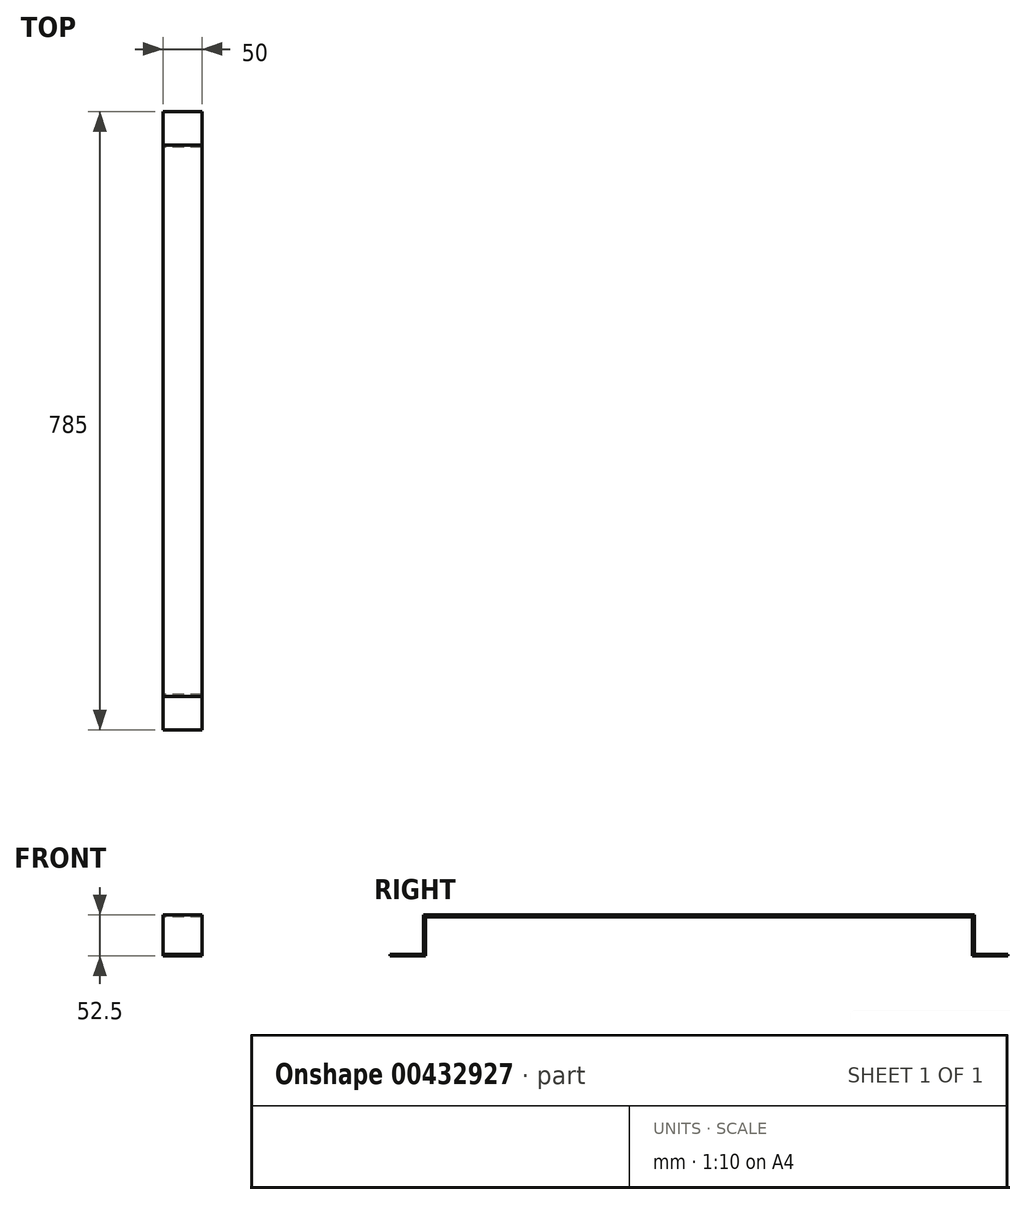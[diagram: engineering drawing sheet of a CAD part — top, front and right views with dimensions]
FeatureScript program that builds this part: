
annotation { "Feature Type Name" : "Feature", "Feature Type Description" : "" }
export const myFeature = defineFeature(function(context is Context, id is Id, definition is map)
    precondition{}
    {
        {
            var Q0;
            Q0=qCreatedBy(makeId("Right.planeOp"),FACE);
            var sketch = newSketch(context, id + "F0", { "sketchPlane" : qUnion([Q0])});
            skLineSegment(sketch, "E0", {"start": v(-392.5, 0) * mm, "end": v(-347.5, 0) * mm});
            skLineSegment(sketch, "E1", {"start": v(-347.5, 0) * mm, "end": v(-347.5, 50) * mm});
            skLineSegment(sketch, "E2", {"start": v(-347.5, 50) * mm, "end": v(0, 50) * mm});
            skLineSegment(sketch, "E3", {"start": v(0, 50) * mm, "end": v(0, 52.5) * mm});
            skLineSegment(sketch, "E4", {"start": v(0, 52.5) * mm, "end": v(-350, 52.5) * mm});
            skLineSegment(sketch, "E5", {"start": v(-350, 52.5) * mm, "end": v(-350, 2.5) * mm});
            skLineSegment(sketch, "E6", {"start": v(-350, 2.5) * mm, "end": v(-392.5, 2.5) * mm});
            skLineSegment(sketch, "E7", {"start": v(-392.5, 2.5) * mm, "end": v(-392.5, 0) * mm});
            skSolve(sketch);
        }
        {
            var Q0;
            Q0 = qSketchRegion(id + "F0", true);
            extrude(context, id + "F1", {"entities" : qUnion([Q0]), "depth" : 50 * mm});
        }
        {
            var Q0;
            Q0=makeQuery(id+"F1.opExtrude","SWEPT_BODY",BODY,{"disambiguationData":[OSD([sQuery(id+"F0.wireOp",EDGE,"E0"),sQuery(id+"F0.wireOp",EDGE,"E1"),sQuery(id+"F0.wireOp",EDGE,"E2"),sQuery(id+"F0.wireOp",EDGE,"E3"),sQuery(id+"F0.wireOp",EDGE,"E4"),sQuery(id+"F0.wireOp",EDGE,"E5"),sQuery(id+"F0.wireOp",EDGE,"E6"),sQuery(id+"F0.wireOp",EDGE,"E7")])]});
            var Q1;
            Q1=qCreatedBy(makeId("Front.planeOp"),FACE);
            mirror(context, id + "F2", {"operationType" : NewBodyOperationType.ADD, "entities" : qUnion([Q0]), "mirrorPlane" : qUnion([Q1])});
        }
    });
